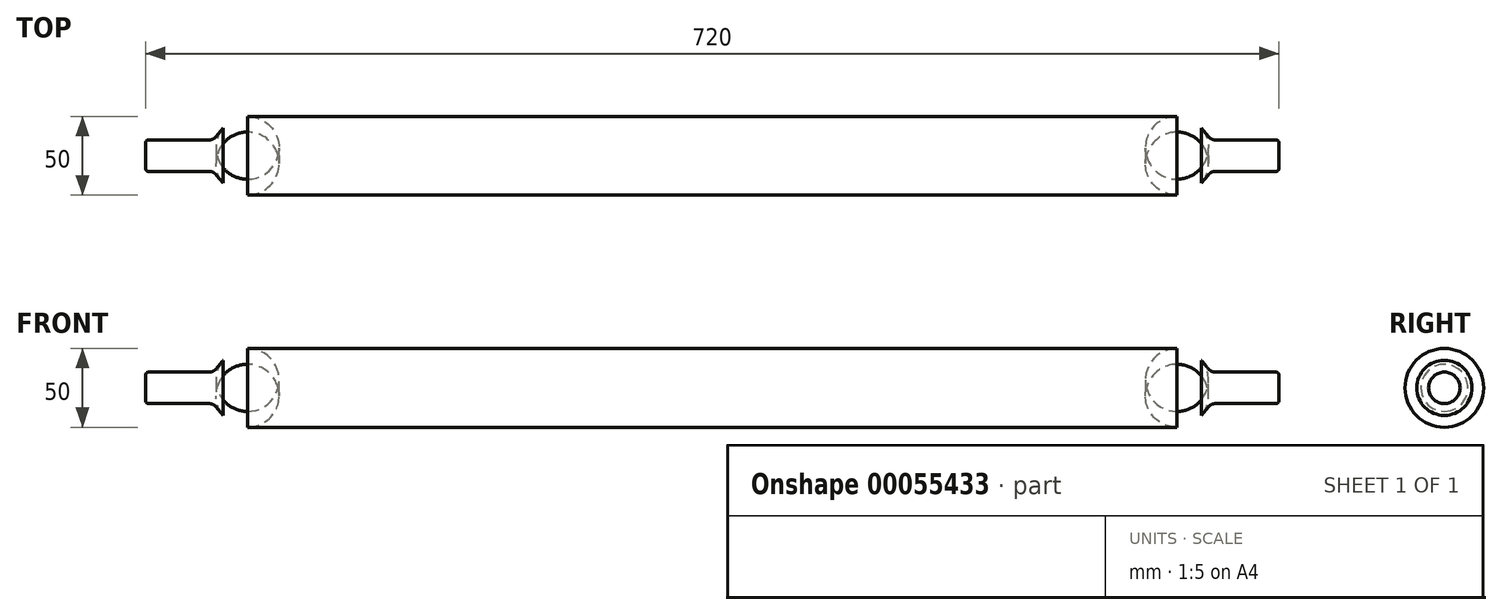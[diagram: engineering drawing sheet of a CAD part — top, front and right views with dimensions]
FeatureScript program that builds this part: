
annotation { "Feature Type Name" : "Feature", "Feature Type Description" : "" }
export const myFeature = defineFeature(function(context is Context, id is Id, definition is map)
    precondition{}
    {
        {
            var Q0;
            Q0=qCreatedBy(makeId("Front.planeOp"),FACE);
            var sketch = newSketch(context, id + "F0", { "sketchPlane" : qUnion([Q0])});
            skLineSegment(sketch, "E0", {"start": v(0, 0) * mm, "end": v(360, 0) * mm, "construction": true});
            skLineSegment(sketch, "E1", {"start": v(0, 0) * mm, "end": v(0, 8) * mm});
            skLineSegment(sketch, "E2", {"start": v(2, 10) * mm, "end": v(40.46, 10) * mm});
            skLineSegment(sketch, "E3", {"start": v(44.98, 12.17) * mm, "end": v(49.26, 17.5) * mm});
            skLineSegment(sketch, "E4", {"start": v(64.86, 25) * mm, "end": v(360, 25) * mm});
            skLineSegment(sketch, "E5", {"start": v(0, 0) * mm, "end": v(360, 0) * mm});
            skArc(sketch, "E6.filletArc", {"start": v(40.46, 10) * mm, "mid": v(42.97, 10.57) * mm, "end": v(44.98, 12.17) * mm});
            skArc(sketch, "E7.filletArc", {"start": v(64.86, 25) * mm, "mid": v(56.2, 23.03) * mm, "end": v(49.26, 17.5) * mm});
            skPoint(sketch, "E8.visualSharp", {"position": v(0, 10) * mm});
            skArc(sketch, "E8.filletArc", {"start": v(2, 10) * mm, "mid": v(0.59, 9.41) * mm, "end": v(0, 8) * mm});
            skLineSegment(sketch, "E9", {"start": v(360, -20.04) * mm, "end": v(360, 43.77) * mm, "construction": true});
            skPoint(sketch, "E9.startSnap0", {"position": v(360, 0) * mm});
            skLineSegment(sketch, "E10.MirrorCS", {"start": v(720, 0) * mm, "end": v(720, 8) * mm});
            skLineSegment(sketch, "E11.MirrorCS", {"start": v(675.02, 12.17) * mm, "end": v(670.74, 17.5) * mm});
            skArc(sketch, "E12.MirrorCS", {"start": v(718, 10) * mm, "mid": v(719.41, 9.41) * mm, "end": v(720, 8) * mm});
            skArc(sketch, "E13.MirrorCS", {"start": v(679.54, 10) * mm, "mid": v(677.03, 10.57) * mm, "end": v(675.02, 12.17) * mm});
            skArc(sketch, "E14.MirrorCS", {"start": v(655.14, 25) * mm, "mid": v(663.8, 23.03) * mm, "end": v(670.74, 17.5) * mm});
            skPoint(sketch, "E15.MirrorP", {"position": v(720, 10) * mm});
            skLineSegment(sketch, "E16.MirrorCS", {"start": v(718, 10) * mm, "end": v(679.54, 10) * mm});
            skLineSegment(sketch, "E17.MirrorCS", {"start": v(655.14, 25) * mm, "end": v(360, 25) * mm});
            skLineSegment(sketch, "E18.MirrorCS", {"start": v(720, 0) * mm, "end": v(360, 0) * mm});
            skSolve(sketch);
        }
        {
            var Q0;
            Q0 = qSketchRegion(id + "F0", true);
            var Q1;
            Q1=sQuery(id+"F0.wireOp",EDGE,"E5");
            revolve(context, id + "F1", {"entities" : qUnion([Q0]), "axis" : qUnion([Q1]), "revolveType" : RevolveType.FULL});
        }
    });
